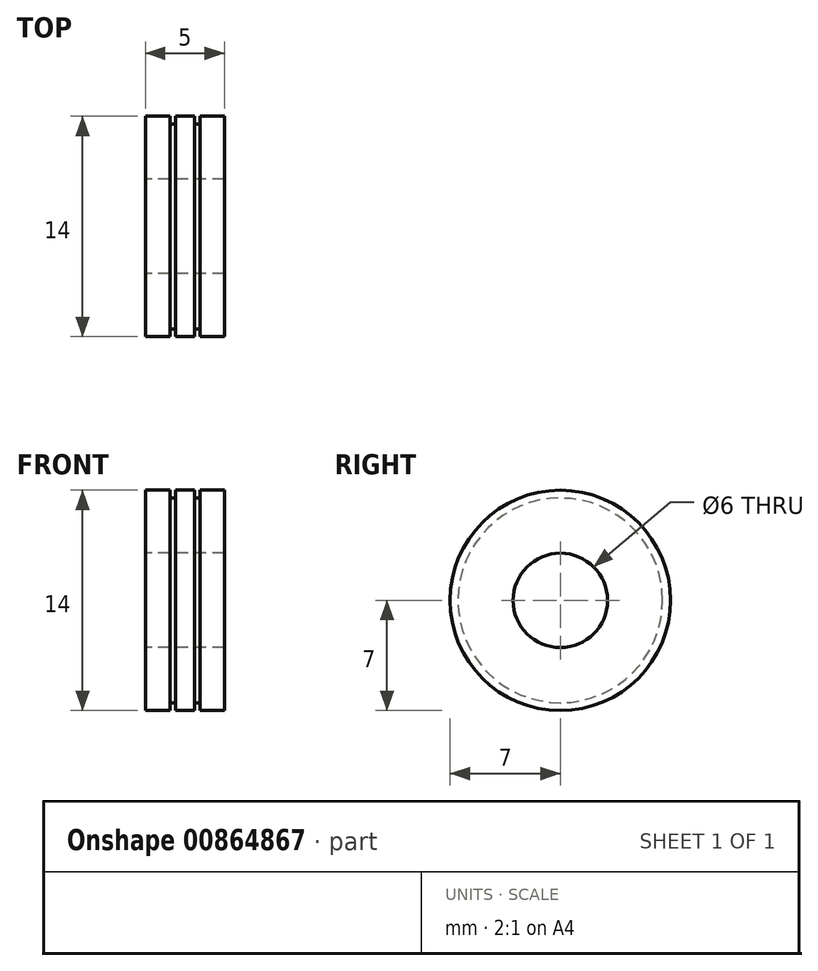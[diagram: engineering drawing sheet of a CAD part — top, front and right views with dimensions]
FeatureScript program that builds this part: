
annotation { "Feature Type Name" : "Feature", "Feature Type Description" : "" }
export const myFeature = defineFeature(function(context is Context, id is Id, definition is map)
    precondition{}
    {
        {
            var Q0;
            Q0=qCreatedBy(makeId("Front.planeOp"),FACE);
            var sketch = newSketch(context, id + "F0", { "sketchPlane" : qUnion([Q0])});
            skLineSegment(sketch, "E0", {"start": v(0, 0) * mm, "end": v(12.38, 0) * mm, "construction": true});
            skLineSegment(sketch, "E1", {"start": v(0, 0) * mm, "end": v(0, 7) * mm});
            skLineSegment(sketch, "E2", {"start": v(0, 7) * mm, "end": v(1.55, 7) * mm});
            skLineSegment(sketch, "E3", {"start": v(1.55, 7) * mm, "end": v(1.55, 6.5) * mm});
            skLineSegment(sketch, "E4", {"start": v(1.55, 6.5) * mm, "end": v(1.9, 6.5) * mm});
            skLineSegment(sketch, "E5", {"start": v(1.9, 6.5) * mm, "end": v(1.9, 7) * mm});
            skLineSegment(sketch, "E6", {"start": v(1.9, 7) * mm, "end": v(3.1, 7) * mm});
            skLineSegment(sketch, "E7", {"start": v(3.1, 7) * mm, "end": v(3.1, 6.5) * mm});
            skLineSegment(sketch, "E8", {"start": v(3.1, 6.5) * mm, "end": v(3.45, 6.5) * mm});
            skLineSegment(sketch, "E9", {"start": v(3.45, 6.5) * mm, "end": v(3.45, 7) * mm});
            skLineSegment(sketch, "E10", {"start": v(3.45, 7) * mm, "end": v(5, 7) * mm});
            skLineSegment(sketch, "E11", {"start": v(5, 7) * mm, "end": v(5, 3) * mm});
            skLineSegment(sketch, "E12", {"start": v(5, 3) * mm, "end": v(0, 3) * mm});
            skLineSegment(sketch, "E13", {"start": v(0, 3) * mm, "end": v(0, 7) * mm});
            skSolve(sketch);
        }
        {
            var Q0;
            Q0=makeQuery(id+"F0.imprint","IMPRINT",FACE,{"disambiguationData":[TD([[makeQuery(id+"F0.imprint","IMPRINT",EDGE,{"derivedFrom":sQuery(id+"F0.wireOp",EDGE,"E2")}),-1.0]])]});
            var Q1;
            Q1=sQuery(id+"F0.wireOp",EDGE,"E0");
            revolve(context, id + "F1", {"surfaceOperationType" : NewSurfaceOperationType.NEW, "entities" : qUnion([Q0]), "axis" : qUnion([Q1]), "revolveType" : RevolveType.FULL});
        }
    });
